# Revit family: U-Bolt Pipe Support
name_source: partatom
category: Pipe Fittings
revit_build: Autodesk Revit 2014 (Build: 20130308_1515(x64)
units: mm (PartAtom-declared; Revit-internal decimal feet)

## types (24) — shared parameters
Fasteners = Fasteners
Neoprene Pad = Rubber
Pipe Support = Pipe Support

## per-type parameters (varying)
| type | Anchor Nut | Dim_C | Dim_D | Nominal Diameter | Nominal Radius | Pipe OD | Pipe Outside Radius | Spring |
| 1200 | Nut : M25 | 50 mm  [stored 0.164042 ft] | 25 mm  [stored 0.082021 ft] | 1200 mm | 600 mm | 1290 mm | 645 mm | Spring |
| 600 | Nut : M16 | 32 mm  [stored 0.104987 ft] | 16 mm  [stored 0.0524934 ft] | 600 mm | 300 mm | 610 mm | 305 mm | <By Category> |
| 300 | Nut : M16 | 32 mm  [stored 0.104987 ft] | 16 mm  [stored 0.0524934 ft] | 300 mm | 150 mm | 324 mm | 162 mm | <By Category> |
| 100 | Nut : M12 | 24 mm  [stored 0.0787402 ft] | 12 mm  [stored 0.0393701 ft] | 100 mm | 50 mm | 114 mm | 57 mm | <By Category> |
| 150 | Nut : M12 | 24 mm  [stored 0.0787402 ft] | 12 mm  [stored 0.0393701 ft] | 150 mm | 75 mm | 168 mm | 84 mm | <By Category> |
| 200 | Nut : M16 | 32 mm  [stored 0.104987 ft] | 16 mm  [stored 0.0524934 ft] | 200 mm | 100 mm | 219 mm | 110 mm | <By Category> |
| 250 | Nut : M16 | 32 mm  [stored 0.104987 ft] | 16 mm  [stored 0.0524934 ft] | 250 mm | 125 mm | 273 mm | 137 mm | <By Category> |
| 350 | Nut : M16 | 32 mm  [stored 0.104987 ft] | 16 mm  [stored 0.0524934 ft] | 350 mm | 175 mm | 356 mm | 178 mm | <By Category> |
| 400 | Nut : M16 | 32 mm  [stored 0.104987 ft] | 16 mm  [stored 0.0524934 ft] | 400 mm | 200 mm | 406 mm | 203 mm | <By Category> |
| 450 | Nut : M16 | 32 mm  [stored 0.104987 ft] | 16 mm  [stored 0.0524934 ft] | 450 mm | 225 mm | 457 mm | 229 mm | <By Category> |
| 500 | Nut : M16 | 32 mm  [stored 0.104987 ft] | 16 mm  [stored 0.0524934 ft] | 500 mm | 250 mm | 508 mm | 254 mm | <By Category> |
| 750 | Nut : M20 | 40 mm  [stored 0.131234 ft] | 20 mm  [stored 0.0656168 ft] | 750 mm | 375 mm | 813 mm | 406 mm | <By Category> |
| 900 | Nut : M20 | 40 mm  [stored 0.131234 ft] | 20 mm  [stored 0.0656168 ft] | 900 mm | 450 mm | 973 mm | 486 mm | <By Category> |
| 1050 | Nut : M25 | 50 mm  [stored 0.164042 ft] | 25 mm  [stored 0.082021 ft] | 1050 mm | 525 mm | 1130 mm | 565 mm | <By Category> |
| 15 | Nut : M6 | 12 mm  [stored 0.0393701 ft] | 6 mm  [stored 0.019685 ft] | 15 mm | 8 mm | 21 mm | 11 mm  [stored 0.0360892 ft] | <By Category> |
| 20 | Nut : M6 | 12 mm  [stored 0.0393701 ft] | 6 mm  [stored 0.019685 ft] | 20 mm | 10 mm | 27 mm | 13 mm | <By Category> |
| 25 | Nut : M6 | 12 mm  [stored 0.0393701 ft] | 6 mm  [stored 0.019685 ft] | 25 mm | 13 mm | 33 mm | 17 mm | <By Category> |
| 32 | Nut : M10 | 20 mm  [stored 0.0656168 ft] | 10 mm  [stored 0.0328084 ft] | 32 mm | 16 mm | 42 mm | 21 mm | <By Category> |
| 40 | Nut : M10 | 20 mm  [stored 0.0656168 ft] | 10 mm  [stored 0.0328084 ft] | 40 mm | 20 mm | 48 mm  [stored 0.15748 ft] | 24 mm  [stored 0.0787402 ft] | <By Category> |
| 50 | Nut : M10 | 20 mm  [stored 0.0656168 ft] | 10 mm  [stored 0.0328084 ft] | 50 mm | 25 mm | 60 mm | 30 mm  [stored 0.0984252 ft] | <By Category> |
| 65 | Nut : M10 | 20 mm  [stored 0.0656168 ft] | 10 mm  [stored 0.0328084 ft] | 65 mm | 33 mm | 73 mm  [stored 0.239501 ft] | 37 mm | <By Category> |
| 80 | Nut : M12 | 24 mm  [stored 0.0787402 ft] | 12 mm  [stored 0.0393701 ft] | 80 mm | 40 mm | 89 mm | 44 mm  [stored 0.144357 ft] | <By Category> |
| 90 | Nut : M12 | 24 mm  [stored 0.0787402 ft] | 12 mm  [stored 0.0393701 ft] | 90 mm | 45 mm | 102 mm | 51 mm | <By Category> |
| 125 | Nut : M12 | 24 mm  [stored 0.0787402 ft] | 12 mm  [stored 0.0393701 ft] | 125 mm | 63 mm | 141 mm | 71 mm | <By Category> |

note: [stored X ft] marks values corroborated as IEEE doubles in the binary element streams (Revit-internal decimal feet)

## geometry (parser evidence)
native form markers: Sweep x5
no freeform markers — native parametric forms only
